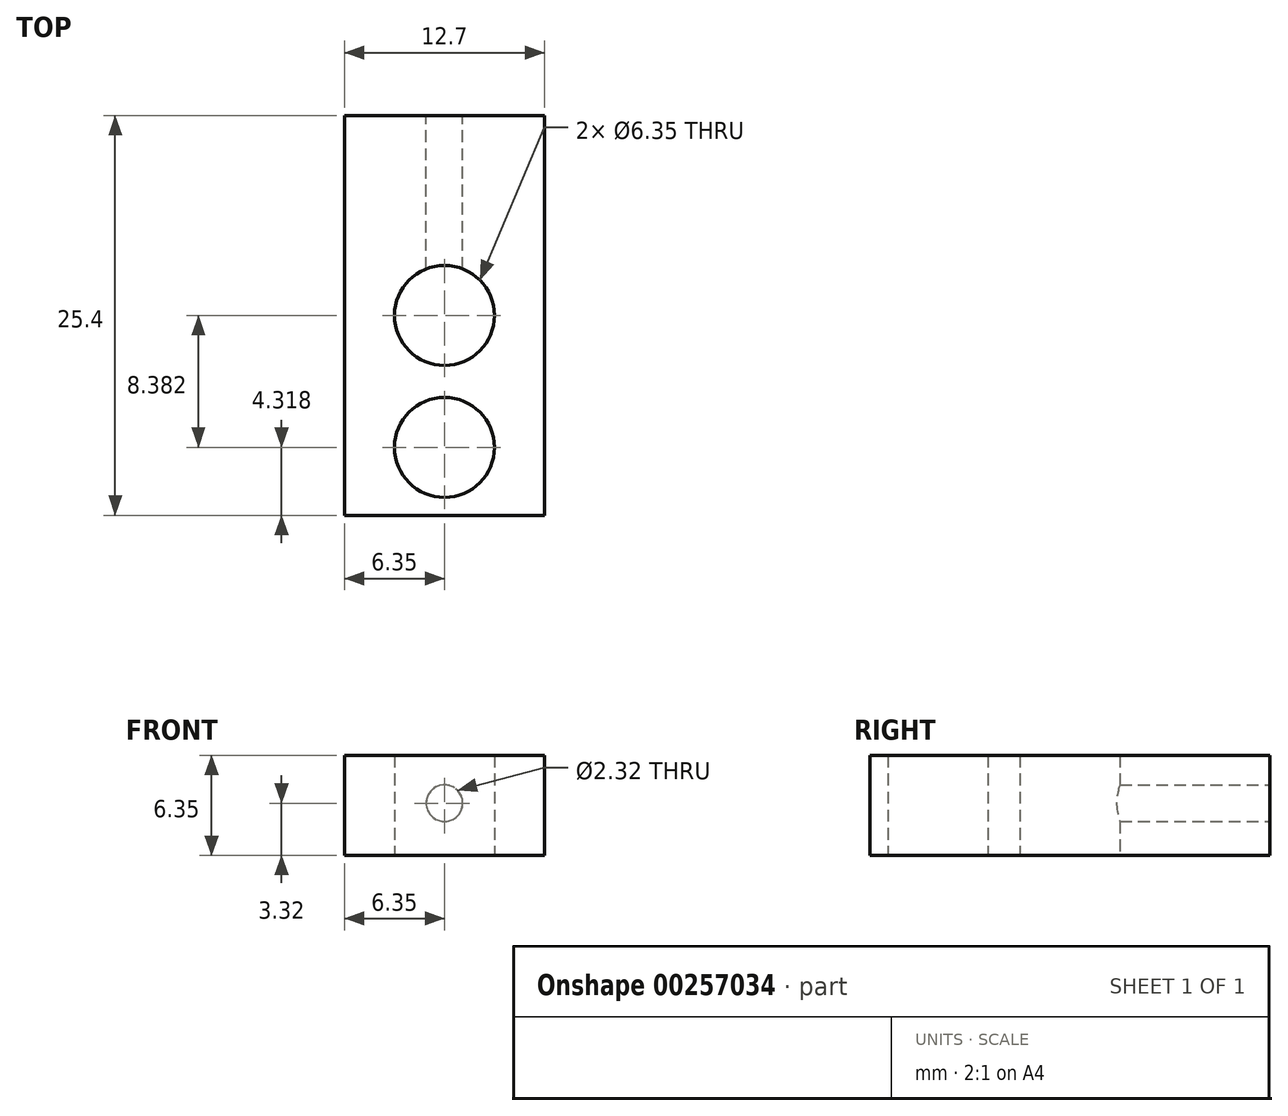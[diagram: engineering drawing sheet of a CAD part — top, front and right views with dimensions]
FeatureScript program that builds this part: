
annotation { "Feature Type Name" : "Feature", "Feature Type Description" : "" }
export const myFeature = defineFeature(function(context is Context, id is Id, definition is map)
    precondition{}
    {
        {
            var Q0;
            Q0=qCreatedBy(makeId("Top.planeOp"),FACE);
            var sketch = newSketch(context, id + "F0", { "sketchPlane" : qUnion([Q0])});
            skLineSegment(sketch, "E0.bottom", {"start": v(6.35, 12.7) * mm, "end": v(-6.35, 12.7) * mm});
            skLineSegment(sketch, "E0.top", {"start": v(6.35, -12.7) * mm, "end": v(-6.35, -12.7) * mm});
            skLineSegment(sketch, "E0.left", {"start": v(6.35, 12.7) * mm, "end": v(6.35, -12.7) * mm});
            skLineSegment(sketch, "E0.right", {"start": v(-6.35, 12.7) * mm, "end": v(-6.35, -12.7) * mm});
            skPoint(sketch, "E0.middle", {"position": v(0, 0) * mm});
            skCircle(sketch, "E1", {"center": v(0, 0) * mm, "radius": 3.18 * mm});
            skCircle(sketch, "E2", {"center": v(0, -8.38) * mm, "radius": 3.18 * mm});
            skSolve(sketch);
        }
        {
            var Q0;
            Q0 = qSketchRegion(id + "F0", true);
            extrude(context, id + "F1", {"entities" : qUnion([Q0]), "depth" : 6.35 * mm});
        }
        {
            var Q0;
            Q0=makeQuery(id+"F1.opExtrude","SWEPT_FACE",FACE,{"disambiguationData":[OSD([sQuery(id+"F0.wireOp",EDGE,"E0.bottom")])]});
            var sketch = newSketch(context, id + "F2", { "sketchPlane" : qUnion([Q0])});
            skCircle(sketch, "E3", {"center": v(0, 3.32) * mm, "radius": 1.16 * mm});
            skSolve(sketch);
        }
        {
            var Q0;
            Q0 = qSketchRegion(id + "F2", true);
            extrude(context, id + "F3", {"entities" : qUnion([Q0]), "operationType" : NewBodyOperationType.REMOVE, "oppositeDirection" : true, "depth" : 10.16 * mm});
        }
    });
